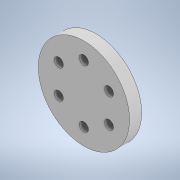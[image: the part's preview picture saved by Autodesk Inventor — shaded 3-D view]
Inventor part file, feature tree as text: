
AUTODESK INVENTOR PART (.ipt)
format: ipt  version: 2020.3 (Build 243373000, 373)  size: 115,712 bytes
history: native  units: mm
features: extrude x2, sketch x2, pattern_circular x1
ambient origin geometry x8: Origin, YZ Plane, XZ Plane, XY Plane, X Axis, Y Axis, Z Axis, Center Point
bodies: Solid1 (feature_tree)
feature tree (5):
  extrude  "Extrusion1"  Depth=4.0mm TaperAngle=0.0deg
  extrude  "Extrusion2"  Depth=10.0mm
  pattern_circular  "Circular Pattern1"  [2 undecoded]
  sketch  "Sketch1"  dims[d0=30.0mm d1=4.0mm d2=0.0mm]
  sketch  "Sketch2"  dims[d3=3.0mm d4=9.525mm d5=10.0mm d6=0.0mm d7=60.0mm d8=360.0deg]
note: 2 required parameter values undecoded (feature->parameter linkage not recoverable at this tier; creation-order binding heuristic only, values carry confidence <= 0.55)
